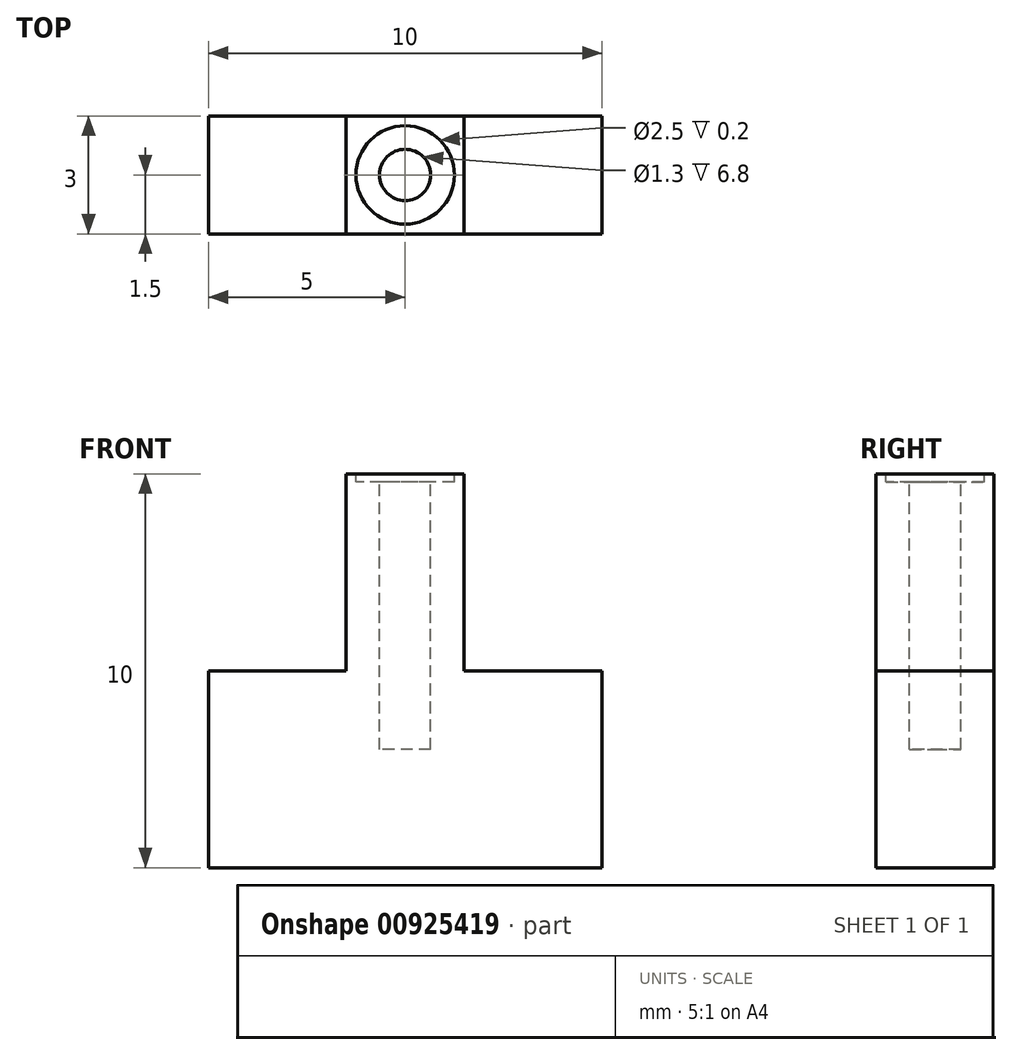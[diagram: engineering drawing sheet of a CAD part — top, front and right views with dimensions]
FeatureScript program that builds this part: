
annotation { "Feature Type Name" : "Feature", "Feature Type Description" : "" }
export const myFeature = defineFeature(function(context is Context, id is Id, definition is map)
    precondition{}
    {
        {
            var Q0;
            Q0=qCreatedBy(makeId("Front.planeOp"),FACE);
            var sketch = newSketch(context, id + "F0", { "sketchPlane" : qUnion([Q0])});
            skLineSegment(sketch, "E0.bottom", {"start": v(5, -2.5) * mm, "end": v(-5, -2.5) * mm});
            skLineSegment(sketch, "E0.top", {"start": v(5, 2.5) * mm, "end": v(1.5, 2.5) * mm});
            skLineSegment(sketch, "E0.left", {"start": v(5, -2.5) * mm, "end": v(5, 2.5) * mm});
            skLineSegment(sketch, "E0.right", {"start": v(-5, -2.5) * mm, "end": v(-5, 2.5) * mm});
            skPoint(sketch, "E0.middle", {"position": v(0, 0) * mm});
            skPoint(sketch, "E1.middle.positionSnap0", {"position": v(0, 2.5) * mm});
            skPoint(sketch, "E1.centerSnap0", {"position": v(0, 2.5) * mm});
            skLineSegment(sketch, "E2.trimOffspring", {"start": v(-1.5, 2.5) * mm, "end": v(-5, 2.5) * mm});
            skLineSegment(sketch, "E3", {"start": v(-1.5, 2.5) * mm, "end": v(1.5, 2.5) * mm});
            skSolve(sketch);
        }
        {
            var Q0;
            Q0 = qSketchRegion(id + "F0", true);
            extrude(context, id + "F1", {"entities" : qUnion([Q0]), "depth" : 3 * mm, "offsetDistance" : 25 * mm});
        }
        {
            var Q0;
            Q0=makeQuery(id+"F1.opExtrude","SWEPT_FACE",FACE,{"disambiguationData":[OSD([sQuery(id+"F0.wireOp",EDGE,"E0.top"),sQuery(id+"F0.wireOp",EDGE,"E2.trimOffspring"),sQuery(id+"F0.wireOp",EDGE,"E3")])]});
            var sketch = newSketch(context, id + "F2", { "sketchPlane" : qUnion([Q0])});
            skLineSegment(sketch, "E4.bottom", {"start": v(1.5, -3) * mm, "end": v(-1.5, -3) * mm});
            skLineSegment(sketch, "E4.top", {"start": v(1.5, 0) * mm, "end": v(-1.5, 0) * mm});
            skLineSegment(sketch, "E4.left", {"start": v(1.5, -3) * mm, "end": v(1.5, 0) * mm});
            skLineSegment(sketch, "E4.right", {"start": v(-1.5, -3) * mm, "end": v(-1.5, 0) * mm});
            skPoint(sketch, "E4.middle", {"position": v(0, -1.5) * mm});
            skPoint(sketch, "E4.middle.positionSnap0", {"position": v(-5, -1.5) * mm});
            skPoint(sketch, "E4.centerSnap0", {"position": v(-5, -1.5) * mm});
            skSolve(sketch);
        }
        {
            var Q0;
            Q0 = qSketchRegion(id + "F2", true);
            extrude(context, id + "F3", {"entities" : qUnion([Q0]), "operationType" : NewBodyOperationType.ADD, "depth" : 5 * mm, "offsetDistance" : 25 * mm});
        }
        {
            var Q0;
            Q0=makeQuery(id+"F3.opExtrude","CAP_FACE",FACE,{"disambiguationData":[OSD([sQuery(id+"F2.wireOp",EDGE,"E4.bottom"),sQuery(id+"F2.wireOp",EDGE,"E4.top"),sQuery(id+"F2.wireOp",EDGE,"E4.left"),sQuery(id+"F2.wireOp",EDGE,"E4.right")])],"isStart":false});
            var sketch = newSketch(context, id + "F4", { "sketchPlane" : qUnion([Q0])});
            skCircle(sketch, "E5", {"center": v(0, -1.5) * mm, "radius": 0.65 * mm});
            skPoint(sketch, "E5.centerSnap0", {"position": v(-1.5, -1.5) * mm});
            skSolve(sketch);
        }
        {
            var Q0;
            Q0 = qSketchRegion(id + "F4", true);
            extrude(context, id + "F5", {"entities" : qUnion([Q0]), "operationType" : NewBodyOperationType.REMOVE, "oppositeDirection" : true, "depth" : 7 * mm, "offsetDistance" : 25 * mm});
        }
        {
            var Q0;
            Q0=makeQuery(id+"F3.opExtrude","CAP_FACE",FACE,{"disambiguationData":[OSD([sQuery(id+"F2.wireOp",EDGE,"E4.bottom"),sQuery(id+"F2.wireOp",EDGE,"E4.top"),sQuery(id+"F2.wireOp",EDGE,"E4.left"),sQuery(id+"F2.wireOp",EDGE,"E4.right")])],"isStart":false});
            var sketch = newSketch(context, id + "F6", { "sketchPlane" : qUnion([Q0])});
            skCircle(sketch, "E6", {"center": v(0, -1.5) * mm, "radius": 1.25 * mm});
            skSolve(sketch);
        }
        {
            var Q0;
            Q0 = qSketchRegion(id + "F6", true);
            extrude(context, id + "F7", {"entities" : qUnion([Q0]), "operationType" : NewBodyOperationType.REMOVE, "oppositeDirection" : true, "depth" : 0.2 * mm, "offsetDistance" : 25 * mm});
        }
    });
